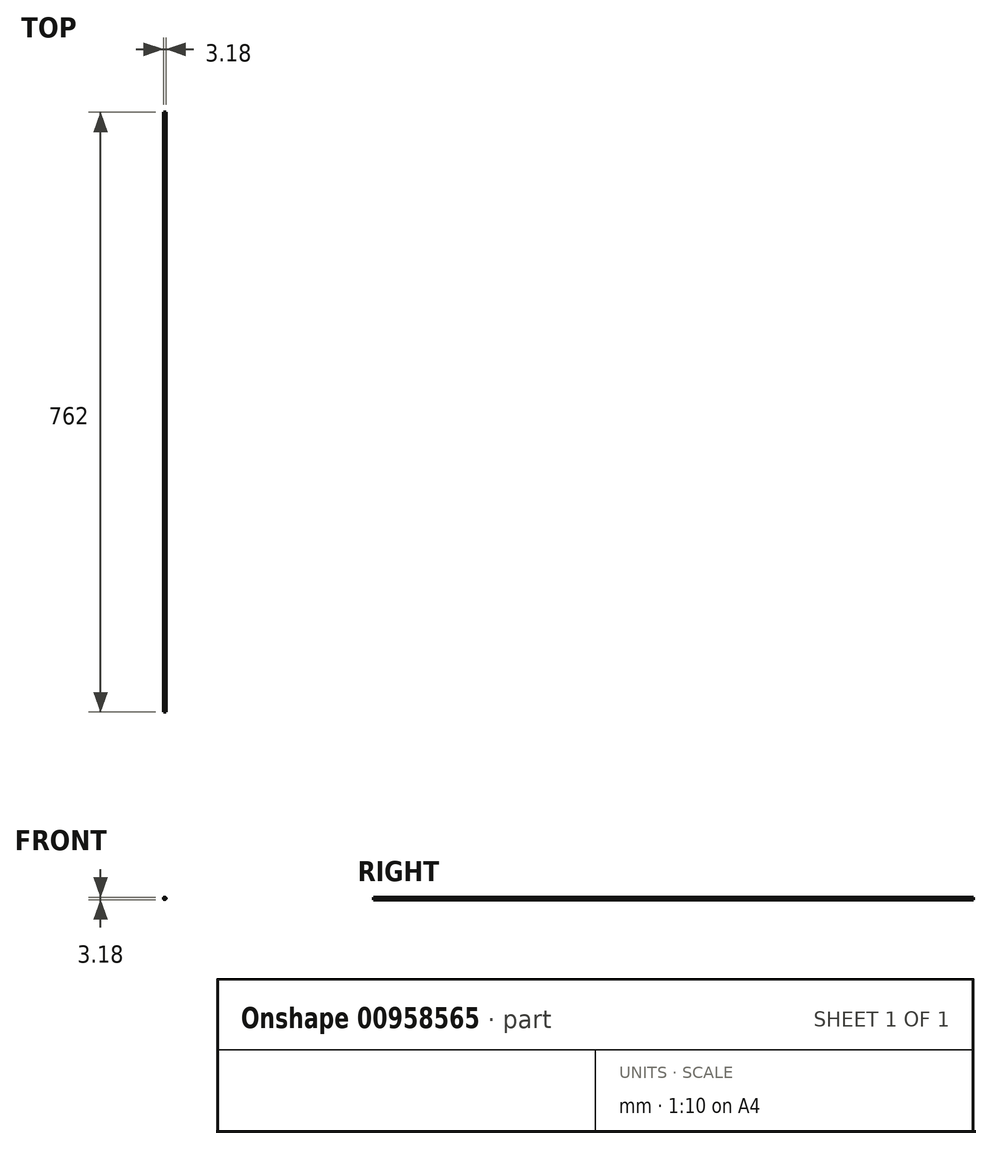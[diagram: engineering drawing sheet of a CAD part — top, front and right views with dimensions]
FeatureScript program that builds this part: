
annotation { "Feature Type Name" : "Feature", "Feature Type Description" : "" }
export const myFeature = defineFeature(function(context is Context, id is Id, definition is map)
    precondition{}
    {
        {
            var Q0;
            Q0=qCreatedBy(makeId("Front.planeOp"),FACE);
            var sketch = newSketch(context, id + "F0", { "sketchPlane" : qUnion([Q0])});
            skCircle(sketch, "E0", {"center": v(0, 0) * mm, "radius": 1.59 * mm});
            skSolve(sketch);
        }
        {
            var Q0;
            Q0=makeQuery(id+"F0.imprint","IMPRINT",FACE,{"disambiguationData":[TD([[makeQuery(id+"F0.imprint","IMPRINT",EDGE,{"derivedFrom":sQuery(id+"F0.wireOp",EDGE,"E0")}),1.0]])]});
            extrude(context, id + "F1", {"entities" : qUnion([Q0]), "depth" : 762 * mm, "offsetDistance" : 25.4 * mm});
        }
    });
